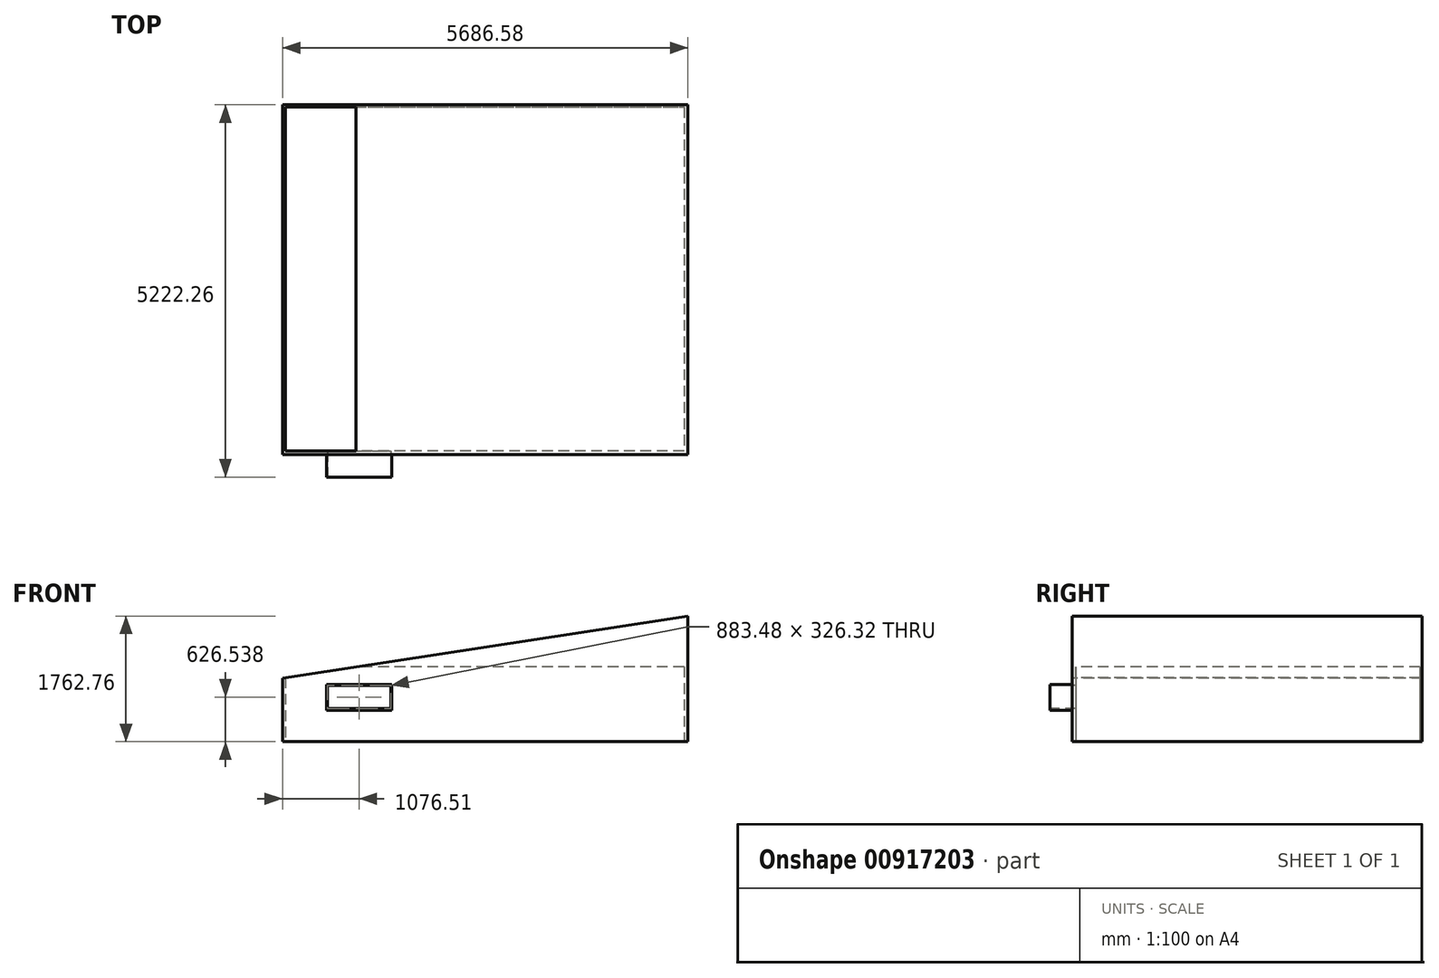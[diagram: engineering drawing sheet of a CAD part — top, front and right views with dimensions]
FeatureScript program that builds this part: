
annotation { "Feature Type Name" : "Feature", "Feature Type Description" : "" }
export const myFeature = defineFeature(function(context is Context, id is Id, definition is map)
    precondition{}
    {
        {
            var Q0;
            Q0=qCreatedBy(makeId("Top.planeOp"),FACE);
            var sketch = newSketch(context, id + "F0", { "sketchPlane" : qUnion([Q0])});
            skLineSegment(sketch, "E0", {"start": v(-2798.84, 2423.93) * mm, "end": v(2789.16, 2423.93) * mm});
            skLineSegment(sketch, "E1", {"start": v(2789.16, 2423.93) * mm, "end": v(2789.16, -2402.07) * mm});
            skLineSegment(sketch, "E2", {"start": v(2789.16, -2402.07) * mm, "end": v(-2798.84, -2402.07) * mm});
            skLineSegment(sketch, "E3", {"start": v(-2798.84, -2402.07) * mm, "end": v(-2798.84, 2423.93) * mm});
            skLineSegment(sketch, "E4", {"start": v(-1528.84, 2423.93) * mm, "end": v(-1528.84, 1128.53) * mm});
            skLineSegment(sketch, "E5", {"start": v(-1528.84, 1128.53) * mm, "end": v(-1827.51, 1128.53) * mm});
            skLineSegment(sketch, "E6", {"start": v(-2137.73, 1128.53) * mm, "end": v(-2798.84, 1128.53) * mm});
            skLineSegment(sketch, "E7", {"start": v(-2801.16, 1200.5) * mm, "end": v(-2137.73, 1200.5) * mm});
            skLineSegment(sketch, "E8", {"start": v(-1830.08, 1200.5) * mm, "end": v(-1600.66, 1200.5) * mm});
            skLineSegment(sketch, "E9", {"start": v(-1600.66, 1200.5) * mm, "end": v(-1600.66, 2423.93) * mm});
            skLineSegment(sketch, "E10", {"start": v(-2843.29, 2453.65) * mm, "end": v(2843.29, 2453.65) * mm});
            skLineSegment(sketch, "E11", {"start": v(2843.29, 2453.65) * mm, "end": v(2843.29, -2453.65) * mm});
            skLineSegment(sketch, "E12", {"start": v(2843.29, -2453.65) * mm, "end": v(-2843.29, -2453.65) * mm});
            skLineSegment(sketch, "E13", {"start": v(-2843.29, -2453.65) * mm, "end": v(-2843.29, 2453.65) * mm});
            skLineSegment(sketch, "E14", {"start": v(-2137.73, 1200.5) * mm, "end": v(-2137.73, 1128.53) * mm});
            skLineSegment(sketch, "E15", {"start": v(-1830.08, 1200.5) * mm, "end": v(-1827.51, 1128.53) * mm});
            skSolve(sketch);
        }
        {
            var Q0;
            Q0=sQuery(id+"F0.wireOp",EDGE,"E6");
            var Q1;
            Q1=sQuery(id+"F0.wireOp",EDGE,"E7");
            var Q2;
            Q2=sQuery(id+"F0.wireOp",EDGE,"E14");
            var Q3;
            Q3=sQuery(id+"F0.wireOp",EDGE,"E8");
            var Q4;
            Q4=sQuery(id+"F0.wireOp",EDGE,"E5");
            var Q5;
            Q5=sQuery(id+"F0.wireOp",EDGE,"E15");
            var Q6;
            Q6=sQuery(id+"F0.wireOp",EDGE,"E9");
            var Q7;
            Q7=sQuery(id+"F0.wireOp",EDGE,"E4");
            extrude(context, id + "F1", {"bodyType" : ToolBodyType.SURFACE, "surfaceEntities" : qUnion([Q0, Q1, Q2, Q3, Q4, Q5, Q6, Q7]), "depth" : 850.9 * mm, "offsetDistance" : 25.4 * mm});
        }
        {
            var Q0;
            Q0 = qSketchRegion(id + "F0", true);
            extrude(context, id + "F2", {"entities" : qUnion([Q0]), "depth" : 1051.56 * mm, "offsetDistance" : 25.4 * mm});
        }
        {
            var Q0;
            Q0=makeQuery(id+"F2.opExtrude","SWEPT_FACE",FACE,{"disambiguationData":[OSD([sQuery(id+"F0.wireOp",EDGE,"E12")])]});
            var sketch = newSketch(context, id + "F3", { "sketchPlane" : qUnion([Q0])});
            skLineSegment(sketch, "E16.bottom", {"start": v(-2221.34, 802.36) * mm, "end": v(-1309.06, 802.36) * mm});
            skLineSegment(sketch, "E16.top", {"start": v(-2221.34, 443.7) * mm, "end": v(-1309.06, 443.7) * mm});
            skLineSegment(sketch, "E16.left", {"start": v(-2221.34, 802.36) * mm, "end": v(-2221.34, 443.7) * mm});
            skLineSegment(sketch, "E16.right", {"start": v(-1309.06, 802.36) * mm, "end": v(-1309.06, 443.7) * mm});
            skSolve(sketch);
        }
        {
            var Q0;
            Q0 = qSketchRegion(id + "F3", true);
            extrude(context, id + "F4", {"entities" : qUnion([Q0]), "operationType" : NewBodyOperationType.ADD, "depth" : 314.96 * mm, "offsetDistance" : 25.4 * mm});
        }
        {
            var Q0;
            Q0=makeQuery(id+"F4.opExtrude","CAP_FACE",FACE,{"disambiguationData":[OSD([sQuery(id+"F3.wireOp",EDGE,"E16.bottom"),sQuery(id+"F3.wireOp",EDGE,"E16.top"),sQuery(id+"F3.wireOp",EDGE,"E16.left"),sQuery(id+"F3.wireOp",EDGE,"E16.right")])],"isStart":false});
            var sketch = newSketch(context, id + "F5", { "sketchPlane" : qUnion([Q0])});
            skLineSegment(sketch, "E17.bottom", {"start": v(-2208.53, 789.7) * mm, "end": v(-1325.04, 789.7) * mm});
            skLineSegment(sketch, "E17.top", {"start": v(-2208.53, 463.38) * mm, "end": v(-1325.04, 463.38) * mm});
            skLineSegment(sketch, "E17.left", {"start": v(-2208.53, 789.7) * mm, "end": v(-2208.53, 463.38) * mm});
            skLineSegment(sketch, "E17.right", {"start": v(-1325.04, 789.7) * mm, "end": v(-1325.04, 463.38) * mm});
            skSolve(sketch);
        }
        {
            var Q0;
            Q0 = qSketchRegion(id + "F5", true);
            extrude(context, id + "F6", {"entities" : qUnion([Q0]), "operationType" : NewBodyOperationType.REMOVE, "oppositeDirection" : true, "depth" : 1803.4 * mm, "offsetDistance" : 25.4 * mm});
        }
        {
            var Q0;
            Q0=makeQuery(id+"F2.opExtrude","CAP_FACE",FACE,{"disambiguationData":[OSD([sQuery(id+"F0.wireOp",EDGE,"E0"),sQuery(id+"F0.wireOp",EDGE,"E1"),sQuery(id+"F0.wireOp",EDGE,"E2"),sQuery(id+"F0.wireOp",EDGE,"E3"),sQuery(id+"F0.wireOp",EDGE,"E10"),sQuery(id+"F0.wireOp",EDGE,"E11"),sQuery(id+"F0.wireOp",EDGE,"E12"),sQuery(id+"F0.wireOp",EDGE,"E13")])],"isStart":false});
            var sketch = newSketch(context, id + "F7", { "sketchPlane" : qUnion([Q0])});
            skLineSegment(sketch, "E18.bottom", {"start": v(-2843.29, 2453.65) * mm, "end": v(2843.29, 2453.65) * mm});
            skLineSegment(sketch, "E18.top", {"start": v(-2843.29, -2453.65) * mm, "end": v(2843.29, -2453.65) * mm});
            skLineSegment(sketch, "E18.left", {"start": v(-2843.29, 2453.65) * mm, "end": v(-2843.29, -2453.65) * mm});
            skLineSegment(sketch, "E18.right", {"start": v(2843.29, 2453.65) * mm, "end": v(2843.29, -2453.65) * mm});
            skSolve(sketch);
        }
        {
            var Q0;
            Q0 = qSketchRegion(id + "F7", true);
            extrude(context, id + "F8", {"entities" : qUnion([Q0]), "operationType" : NewBodyOperationType.ADD, "depth" : 711.2 * mm, "offsetDistance" : 25.4 * mm});
        }
        {
            var Q0;
            Q0=makeQuery(id+"F8.boolean.opBoolean","MERGE",FACE,{"derivedFrom":[makeQuery(id+"F2.opExtrude","SWEPT_FACE",FACE,{"disambiguationData":[OSD([sQuery(id+"F0.wireOp",EDGE,"E12")])]}),makeQuery(id+"F8.opExtrude","SWEPT_FACE",FACE,{"disambiguationData":[OSD([sQuery(id+"F7.wireOp",EDGE,"E18.top")])]})]});
            var sketch = newSketch(context, id + "F9", { "sketchPlane" : qUnion([Q0])});
            skLineSegment(sketch, "E19", {"start": v(-2926.68, 881.38) * mm, "end": v(2843.29, 1762.76) * mm});
            skPoint(sketch, "E19.startSnap0", {"position": v(-2843.29, 881.38) * mm});
            skLineSegment(sketch, "E20", {"start": v(2843.29, 1762.76) * mm, "end": v(-2843.29, 1762.76) * mm});
            skLineSegment(sketch, "E21", {"start": v(-2843.29, 1762.76) * mm, "end": v(-2843.29, 881.38) * mm});
            skSolve(sketch);
        }
        {
            var Q0;
            Q0 = qSketchRegion(id + "F9", true);
            extrude(context, id + "F10", {"entities" : qUnion([Q0]), "operationType" : NewBodyOperationType.REMOVE, "oppositeDirection" : true, "depth" : 6418.58 * mm, "offsetDistance" : 25.4 * mm});
        }
    });
